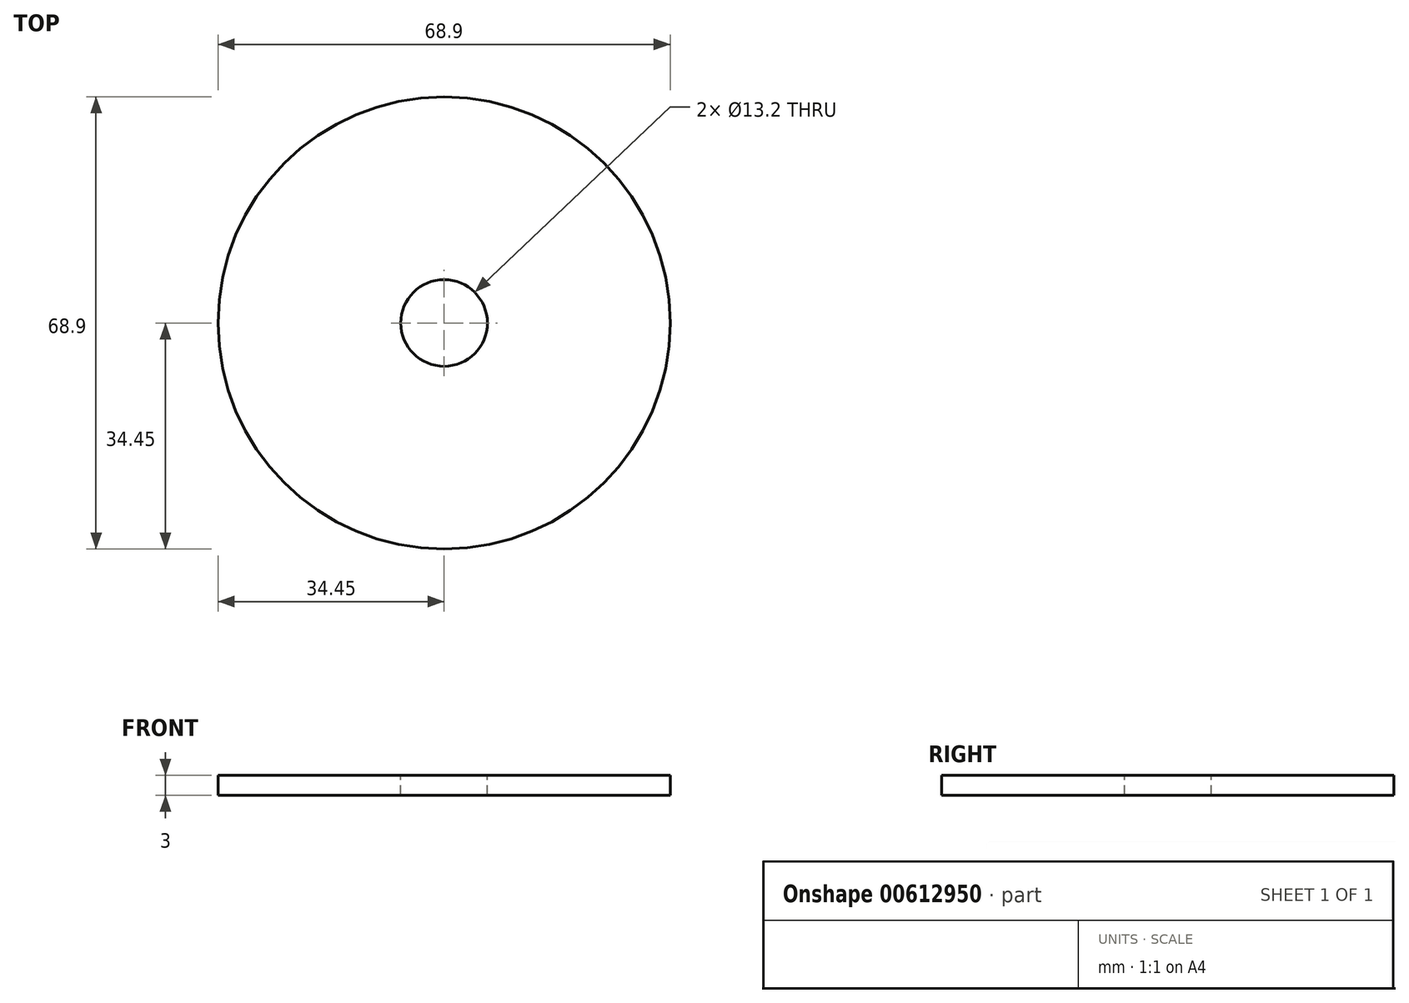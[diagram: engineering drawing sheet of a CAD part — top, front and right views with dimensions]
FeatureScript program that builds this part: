
annotation { "Feature Type Name" : "Feature", "Feature Type Description" : "" }
export const myFeature = defineFeature(function(context is Context, id is Id, definition is map)
    precondition{}
    {
        {
            var Q0;
            Q0=qCreatedBy(makeId("Top.planeOp"),FACE);
            var sketch = newSketch(context, id + "F0", { "sketchPlane" : qUnion([Q0])});
            skCircle(sketch, "E0", {"center": v(0, 0) * mm, "radius": 34.45 * mm});
            skSolve(sketch);
        }
        {
            var Q0;
            Q0=makeQuery(id+"F0.imprint","IMPRINT",FACE,{"disambiguationData":[TD([[makeQuery(id+"F0.imprint","IMPRINT",EDGE,{"derivedFrom":sQuery(id+"F0.wireOp",EDGE,"E0")}),1.0]])]});
            var Q1;
            Q1 = qSketchRegion(id + "FGpqzCAi0RanXPu_0", true);
            extrude(context, id + "F1", {"entities" : qUnion([Q0, Q1]), "oppositeDirection" : true, "depth" : 3 * mm, "offsetDistance" : 25 * mm});
        }
        {
            var Q0;
            Q0=qCreatedBy(makeId("Top.planeOp"),FACE);
            var sketch = newSketch(context, id + "F2", { "sketchPlane" : qUnion([Q0])});
            skPoint(sketch, "E1", {"position": v(0, 0) * mm});
            skSolve(sketch);
        }
        {
            var Q0;
            Q0=sQuery(id+"F2.wireOp",VERTEX,"E1");
            var Q1;
            Q1=makeQuery(id+"F1.opExtrude","SWEPT_BODY",BODY,{"disambiguationData":[OSD([sQuery(id+"F0.wireOp",EDGE,"E0")])]});
            hole(context, id + "F3", {"style" : HoleStyle.SIMPLE, "endStyle" : HoleEndStyle.THROUGH, "standardTappedOrClearance" : lookupTablePath({ "standard" : "ISO", "fit" : "Normal", "size" : "M12", "type" : "Clearance" }), "standardBlindInLast" : lookupTablePath({ "fit" : "Standard", "standard" : "ISO", "size" : "M12", "type" : "Clearance" }), "holeDiameter" : 13.2 * mm, "majorDiameter" : 5 * mm, "isTappedThrough" : true, "tappedDepth" : 12 * mm, "tapClearance" : 3, "locations" : qUnion([Q0]), "scope" : qUnion([Q1])});
        }
        {
            var Q0;
            Q0=makeQuery(id+"F1.opExtrude","SWEPT_BODY",BODY,{"disambiguationData":[OSD([sQuery(id+"F0.wireOp",EDGE,"E0")])]});
            transform(context, id + "F4", {"entities" : qUnion([Q0]), "transformType" : TransformType.TRANSLATION_3D, "dx" : 0 * mm, "dy" : 0 * mm, "dz" : 0 * mm, "makeCopy" : true});
        }
        {
            var Q0;
            Q0=makeQuery(id+"F4.opPattern","COPY",BODY,{"derivedFrom":makeQuery(id+"F1.opExtrude","SWEPT_BODY",BODY,{"disambiguationData":[OSD([sQuery(id+"F0.wireOp",EDGE,"E0")])]}),"instanceName":"1"});
            deleteBodies(context, id + "F5", {"entities" : qUnion([Q0])});
        }
        {
            var Q0;
            Q0=makeQuery(id+"F1.opExtrude","SWEPT_BODY",BODY,{"disambiguationData":[OSD([sQuery(id+"F0.wireOp",EDGE,"E0")])]});
            transform(context, id + "F6", {"entities" : qUnion([Q0]), "transformType" : TransformType.TRANSLATION_3D, "dx" : 0 * mm, "dy" : 0 * mm, "dz" : 0 * mm, "makeCopy" : true});
        }
    });
